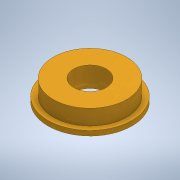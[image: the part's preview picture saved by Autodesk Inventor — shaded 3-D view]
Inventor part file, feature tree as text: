
AUTODESK INVENTOR PART (.ipt)
format: ipt  version: 2020.2 (Build 242310000, 310)  size: 109,056 bytes
history: native  units: mm
features: extrude x2, other x1, sketch x1
ambient origin geometry x8: Origin, YZ Plane, XZ Plane, XY Plane, X Axis, Y Axis, Z Axis, Center Point
bodies: Body1 (feature_tree)
feature tree (4):
  other  "ソリッド1"
  sketch  "スケッチ1"
  extrude  "押し出し1"  Depth=4.0mm
  extrude  "押し出し2"  Depth=9.0mm
